# Revit family: 931-10-001 DN350-900
name_source: partatom
category: Pipe Accessories
units: mm (PartAtom-declared; Revit-internal decimal feet)

## family parameters
Always vertical = Yes
Cut with Voids When Loaded = No
Part Type = Valve - Breaks Into
Round Connector Dimension = Use Diameter
Shared = No
Work Plane-Based = No

## types (16) — shared parameters
1 = 1 mm  [stored 0.00328084 ft]
2 = 3 mm  [stored 0.00984252 ft]
Body_Thickness = 2 mm  [stored 0.00656168 ft]
DN350_PN10 = 931-350-10-010020200000
DN350_PN16 = 931-350-10-020020200000
DN400_PN10 = 931-400-10-010020200000
DN400_PN16 = 931-400-10-020020200000
DN500_PN10 = 931-500-10-010020200000
DN500_PN16 = 931-500-10-020020200000
DN600_PN10 = 931-600-10-010020200000
DN600_PN16 = 931-600-10-020020200000
DN700_PN10 = 931-700-10-010020200000
DN700_PN16 = 931-700-10-020020200000
DN750_PN10 = 931-750-10-010020200000
DN750_PN16 = 931-750-10-020020200000
DN800_PN10 = 931-800-10-010020200000
DN800_PN16 = 931-800-10-020020200000
DN900_PN10 = 931-900-10-010020200000
DN900_PN16 = 931-900-10-020020200000
Description_ = AVK BUTTERFLY VALVE, WAFER, PN10/16
Search_table = 931-10-001 DN350-900
URL_product_pages = https://www.avkvalves.com
zero-valued in all types: Default Elevation

## per-type parameters (varying)
- DN350_PN10: Actuator_FL_T=20 mm  [stored 0.0656168 ft]; Actuator_Flange_R=75 mm; B=174 mm; B1=175 mm; Body_dim=38 mm  [stored 0.124672 ft]; Body_dim1=55 mm  [stored 0.180446 ft]; Body_thickness=184 mm; Bore_R=175 mm; C=78 mm; D=213 mm; D1=426 mm; DN=350 mm; E=306 mm; F=32 mm  [stored 0.104987 ft]; Flange_R=200 mm; Flange_T=25 mm  [stored 0.082021 ft]; G=27 mm  [stored 0.0885827 ft]; H=88 mm; Hole=30 mm  [stored 0.0984252 ft]; Hole_dia=28 mm  [stored 0.0918635 ft]; PCD_R=235 mm; Rib_dim1=250 mm; base=27 mm  [stored 0.0885827 ft]; base1=16 mm; base_dis=247 mm; disk=14 mm  [stored 0.0459318 ft]; disk1=24 mm; disk2=348 mm; hole1=14 mm  [stored 0.0459318 ft]; hole_bottom=210 mm; rib2=235 mm; rubber=19 mm  [stored 0.062336 ft]; wafer=113 mm; wafer_F=40 mm  [stored 0.131234 ft]; wafer_dim1=25 mm  [stored 0.082021 ft]; wafer_dim2=113 mm; wafer_fillet=56 mm
- DN350_PN16: Actuator_FL_T=20 mm  [stored 0.0656168 ft]; Actuator_Flange_R=75 mm; B=174 mm; B1=175 mm; Body_dim=38 mm  [stored 0.124672 ft]; Body_dim1=55 mm  [stored 0.180446 ft]; Body_thickness=184 mm; Bore_R=175 mm; C=78 mm; D=213 mm; D1=426 mm; DN=350 mm; E=306 mm; F=32 mm  [stored 0.104987 ft]; Flange_R=200 mm; Flange_T=27 mm  [stored 0.0885827 ft]; G=27 mm  [stored 0.0885827 ft]; H=88 mm; Hole=30 mm  [stored 0.0984252 ft]; Hole_dia=28 mm  [stored 0.0918635 ft]; PCD_R=235 mm; Rib_dim1=250 mm; base=27 mm  [stored 0.0885827 ft]; base1=16 mm; base_dis=247 mm; disk=14 mm  [stored 0.0459318 ft]; disk1=24 mm; disk2=348 mm; hole1=14 mm  [stored 0.0459318 ft]; hole_bottom=210 mm; rib2=235 mm; rubber=19 mm  [stored 0.062336 ft]; wafer=113 mm; wafer_F=40 mm  [stored 0.131234 ft]; wafer_dim1=27 mm  [stored 0.0885827 ft]; wafer_dim2=113 mm; wafer_fillet=56 mm
- DN400_PN10: Actuator_FL_T=20 mm  [stored 0.0656168 ft]; Actuator_Flange_R=75 mm; B=195 mm; B1=196 mm; Body_dim=38 mm  [stored 0.124672 ft]; Body_dim1=71 mm; Body_thickness=206 mm; Bore_R=200 mm; C=102 mm; D=242 mm; D1=484 mm; DN=400 mm; E=328 mm; F=43 mm  [stored 0.141076 ft]; Flange_R=228 mm; Flange_T=25 mm  [stored 0.082021 ft]; G=27 mm  [stored 0.0885827 ft]; H=88 mm; Hole=30 mm  [stored 0.0984252 ft]; Hole_dia=28 mm  [stored 0.0918635 ft]; PCD_R=258 mm; Rib_dim1=295 mm; base=36 mm  [stored 0.11811 ft]; base1=20 mm  [stored 0.0656168 ft]; base_dis=279 mm; disk=14 mm  [stored 0.0459318 ft]; disk1=24 mm; disk2=390 mm; hole1=14 mm  [stored 0.0459318 ft]; hole_bottom=237 mm; rib2=265 mm; rubber=21 mm  [stored 0.0688976 ft]; wafer=113 mm; wafer_F=40 mm  [stored 0.131234 ft]; wafer_dim1=25 mm  [stored 0.082021 ft]; wafer_dim2=113 mm; wafer_fillet=56 mm
- DN400_PN16: Actuator_FL_T=20 mm  [stored 0.0656168 ft]; Actuator_Flange_R=75 mm; B=195 mm; B1=196 mm; Body_dim=38 mm  [stored 0.124672 ft]; Body_dim1=71 mm; Body_thickness=206 mm; Bore_R=200 mm; C=102 mm; D=242 mm; D1=484 mm; DN=400 mm; E=328 mm; F=43 mm  [stored 0.141076 ft]; Flange_R=230 mm; Flange_T=28 mm  [stored 0.0918635 ft]; G=27 mm  [stored 0.0885827 ft]; H=88 mm; Hole=30 mm  [stored 0.0984252 ft]; Hole_dia=28 mm  [stored 0.0918635 ft]; PCD_R=263 mm; Rib_dim1=295 mm; base=36 mm  [stored 0.11811 ft]; base1=20 mm  [stored 0.0656168 ft]; base_dis=279 mm; disk=14 mm  [stored 0.0459318 ft]; disk1=24 mm; disk2=390 mm; hole1=14 mm  [stored 0.0459318 ft]; hole_bottom=237 mm; rib2=265 mm; rubber=21 mm  [stored 0.0688976 ft]; wafer=113 mm; wafer_F=40 mm  [stored 0.131234 ft]; wafer_dim1=28 mm  [stored 0.0918635 ft]; wafer_dim2=113 mm; wafer_fillet=56 mm
- DN500_PN10: Actuator_FL_T=20 mm  [stored 0.0656168 ft]; Actuator_Flange_R=88 mm; B=246 mm; B1=247 mm; Body_dim=44 mm; Body_dim1=89 mm; Body_thickness=259 mm; Bore_R=250 mm; C=127 mm; D=299 mm; D1=597 mm; DN=500 mm; E=403 mm; F=39 mm  [stored 0.127953 ft]; Flange_R=285 mm; Flange_T=27 mm  [stored 0.0885827 ft]; G=36 mm  [stored 0.11811 ft]; H=105 mm; Hole=40 mm  [stored 0.131234 ft]; Hole_dia=31 mm  [stored 0.101706 ft]; PCD_R=310 mm; Rib_dim1=349 mm; base=44 mm; base1=25 mm  [stored 0.082021 ft]; base_dis=349 mm; disk=18 mm  [stored 0.0590551 ft]; disk1=32 mm  [stored 0.104987 ft]; disk2=492 mm; hole1=18 mm  [stored 0.0590551 ft]; hole_bottom=297 mm; rib2=332 mm; rubber=24 mm; wafer=131 mm; wafer_F=41 mm  [stored 0.134514 ft]; wafer_dim1=27 mm  [stored 0.0885827 ft]; wafer_dim2=131 mm; wafer_fillet=66 mm
- DN500_PN16: Actuator_FL_T=18 mm  [stored 0.0590551 ft]; Actuator_Flange_R=88 mm; B=246 mm; B1=247 mm; Body_dim=44 mm; Body_dim1=89 mm; Body_thickness=259 mm; Bore_R=250 mm; C=127 mm; D=299 mm; D1=597 mm; DN=500 mm; E=403 mm; F=39 mm  [stored 0.127953 ft]; Flange_R=300 mm; Flange_T=32 mm  [stored 0.104987 ft]; G=36 mm  [stored 0.11811 ft]; H=105 mm; Hole=40 mm  [stored 0.131234 ft]; Hole_dia=31 mm  [stored 0.101706 ft]; PCD_R=310 mm; Rib_dim1=349 mm; base=44 mm; base1=25 mm  [stored 0.082021 ft]; base_dis=349 mm; disk=18 mm  [stored 0.0590551 ft]; disk1=32 mm  [stored 0.104987 ft]; disk2=492 mm; hole1=18 mm  [stored 0.0590551 ft]; hole_bottom=297 mm; rib2=332 mm; rubber=24 mm; wafer=131 mm; wafer_F=41 mm  [stored 0.134514 ft]; wafer_dim1=32 mm  [stored 0.104987 ft]; wafer_dim2=131 mm; wafer_fillet=66 mm
- DN600_PN10: Actuator_FL_T=30 mm  [stored 0.0984252 ft]; Actuator_Flange_R=105 mm; B=289 mm; B1=290 mm; Body_dim=53 mm; Body_dim1=108 mm; Body_thickness=304 mm; Bore_R=300 mm; C=154 mm; D=359 mm; D1=717 mm; DN=600 mm; E=495 mm; F=68 mm; Flange_R=350 mm; Flange_T=30 mm  [stored 0.0984252 ft]; G=46 mm  [stored 0.150919 ft]; H=105 mm; Hole=51 mm; Hole_dia=31 mm  [stored 0.101706 ft]; PCD_R=363 mm; Rib_dim1=432 mm; base=54 mm; base1=31 mm  [stored 0.101706 ft]; base_dis=432 mm; disk=23 mm  [stored 0.0754593 ft]; disk1=41 mm  [stored 0.134514 ft]; disk2=577 mm; hole1=23 mm  [stored 0.0754593 ft]; hole_bottom=367 mm; rib2=410 mm; rubber=29 mm; wafer=158 mm; wafer_F=41 mm  [stored 0.134514 ft]; wafer_dim1=30 mm  [stored 0.0984252 ft]; wafer_dim2=158 mm; wafer_fillet=79 mm
- DN600_PN16: Actuator_FL_T=30 mm  [stored 0.0984252 ft]; Actuator_Flange_R=105 mm; B=289 mm; B1=290 mm; Body_dim=53 mm; Body_dim1=108 mm; Body_thickness=304 mm; Bore_R=300 mm; C=154 mm; D=359 mm; D1=717 mm; DN=600 mm; E=495 mm; F=68 mm; Flange_R=350 mm; Flange_T=36 mm  [stored 0.11811 ft]; G=46 mm  [stored 0.150919 ft]; H=105 mm; Hole=51 mm; Hole_dia=37 mm  [stored 0.121391 ft]; PCD_R=363 mm; Rib_dim1=432 mm; base=54 mm; base1=31 mm  [stored 0.101706 ft]; base_dis=432 mm; disk=23 mm  [stored 0.0754593 ft]; disk1=41 mm  [stored 0.134514 ft]; disk2=577 mm; hole1=23 mm  [stored 0.0754593 ft]; hole_bottom=367 mm; rib2=410 mm; rubber=29 mm; wafer=158 mm; wafer_F=41 mm  [stored 0.134514 ft]; wafer_dim1=36 mm  [stored 0.11811 ft]; wafer_dim2=158 mm; wafer_fillet=79 mm
- DN700_PN10: Actuator_FL_T=30 mm  [stored 0.0984252 ft]; Actuator_Flange_R=105 mm; B=341 mm; B1=342 mm; Body_dim=53 mm; Body_dim1=116 mm; Body_thickness=359 mm; Bore_R=350 mm; C=165 mm; D=397 mm; D1=793 mm; DN=700 mm; E=565 mm; F=68 mm; Flange_R=410 mm; Flange_T=33 mm  [stored 0.108268 ft]; G=46 mm  [stored 0.150919 ft]; H=105 mm; Hole=51 mm; Hole_dia=36 mm  [stored 0.11811 ft]; PCD_R=430 mm; Rib_dim1=500 mm; base=58 mm; base1=33 mm  [stored 0.108268 ft]; base_dis=500 mm; disk=23 mm  [stored 0.0754593 ft]; disk1=41 mm  [stored 0.134514 ft]; disk2=681 mm; hole1=23 mm  [stored 0.0754593 ft]; hole_bottom=425 mm; rib2=475 mm; rubber=23 mm  [stored 0.0754593 ft]; wafer=158 mm; wafer_F=45 mm  [stored 0.147638 ft]; wafer_dim1=33 mm  [stored 0.108268 ft]; wafer_dim2=158 mm; wafer_fillet=79 mm
- DN700_PN16: Actuator_FL_T=30 mm  [stored 0.0984252 ft]; Actuator_Flange_R=105 mm; B=341 mm; B1=342 mm; Body_dim=53 mm; Body_dim1=116 mm; Body_thickness=359 mm; Bore_R=350 mm; C=165 mm; D=397 mm; D1=793 mm; DN=700 mm; E=565 mm; F=68 mm; Flange_R=410 mm; Flange_T=40 mm  [stored 0.131234 ft]; G=46 mm  [stored 0.150919 ft]; H=105 mm; Hole=51 mm; Hole_dia=36 mm  [stored 0.11811 ft]; PCD_R=420 mm; Rib_dim1=500 mm; base=58 mm; base1=33 mm  [stored 0.108268 ft]; base_dis=500 mm; disk=23 mm  [stored 0.0754593 ft]; disk1=41 mm  [stored 0.134514 ft]; disk2=681 mm; hole1=23 mm  [stored 0.0754593 ft]; hole_bottom=425 mm; rib2=475 mm; rubber=23 mm  [stored 0.0754593 ft]; wafer=158 mm; wafer_F=45 mm  [stored 0.147638 ft]; wafer_dim1=40 mm  [stored 0.131234 ft]; wafer_dim2=158 mm; wafer_fillet=79 mm
- DN750_PN10: Actuator_FL_T=30 mm  [stored 0.0984252 ft]; Actuator_Flange_R=105 mm; B=372 mm; B1=373 mm; Body_dim=53 mm; Body_dim1=116 mm; Body_thickness=391 mm; Bore_R=375 mm; C=165 mm; D=438 mm; D1=875 mm; DN=750 mm; E=584 mm; F=68 mm; Flange_R=430 mm; Flange_T=40 mm  [stored 0.131234 ft]; G=46 mm  [stored 0.150919 ft]; H=105 mm; Hole=51 mm; Hole_dia=31 mm  [stored 0.101706 ft]; PCD_R=457 mm; Rib_dim1=500 mm; base=58 mm; base1=33 mm  [stored 0.108268 ft]; base_dis=530 mm; disk=23 mm  [stored 0.0754593 ft]; disk1=41 mm  [stored 0.134514 ft]; disk2=743 mm; hole1=23 mm  [stored 0.0754593 ft]; hole_bottom=451 mm; rib2=504 mm; rubber=31 mm  [stored 0.101706 ft]; wafer=158 mm; wafer_F=46 mm  [stored 0.150919 ft]; wafer_dim1=40 mm  [stored 0.131234 ft]; wafer_dim2=158 mm; wafer_fillet=79 mm
- DN750_PN16: Actuator_FL_T=30 mm  [stored 0.0984252 ft]; Actuator_Flange_R=105 mm; B=372 mm; B1=373 mm; Body_dim=53 mm; Body_dim1=116 mm; Body_thickness=391 mm; Bore_R=375 mm; C=165 mm; D=438 mm; D1=875 mm; DN=750 mm; E=584 mm; F=68 mm; Flange_R=425 mm; Flange_T=40 mm  [stored 0.131234 ft]; G=46 mm  [stored 0.150919 ft]; H=105 mm; Hole=51 mm; Hole_dia=31 mm  [stored 0.101706 ft]; PCD_R=457 mm; Rib_dim1=500 mm; base=58 mm; base1=33 mm  [stored 0.108268 ft]; base_dis=530 mm; disk=23 mm  [stored 0.0754593 ft]; disk1=41 mm  [stored 0.134514 ft]; disk2=743 mm; hole1=23 mm  [stored 0.0754593 ft]; hole_bottom=451 mm; rib2=504 mm; rubber=31 mm  [stored 0.101706 ft]; wafer=158 mm; wafer_F=46 mm  [stored 0.150919 ft]; wafer_dim1=40 mm  [stored 0.131234 ft]; wafer_dim2=158 mm; wafer_fillet=79 mm
- DN800_PN10: Actuator_FL_T=32 mm  [stored 0.104987 ft]; Actuator_Flange_R=150 mm; B=394 mm; B1=395 mm; Body_dim=75 mm; Body_dim1=133 mm; Body_thickness=414 mm; Bore_R=400 mm; C=190 mm; D=454 mm; D1=907 mm; DN=800 mm; E=645 mm; F=75 mm; Flange_R=460 mm; Flange_T=35 mm  [stored 0.114829 ft]; G=55 mm  [stored 0.180446 ft]; H=150 mm; Hole=61 mm; Hole_dia=34 mm  [stored 0.111549 ft]; PCD_R=475 mm; Rib_dim1=540 mm; base=67 mm; base1=38 mm  [stored 0.124672 ft]; base_dis=551 mm; disk=28 mm  [stored 0.0918635 ft]; disk1=50 mm; disk2=787 mm; hole1=28 mm  [stored 0.0918635 ft]; hole_bottom=468 mm; rib2=523 mm; rubber=27 mm  [stored 0.0885827 ft]; wafer=225 mm; wafer_F=72 mm; wafer_dim1=35 mm  [stored 0.114829 ft]; wafer_dim2=225 mm; wafer_fillet=113 mm
- DN800_PN16: Actuator_FL_T=32 mm  [stored 0.104987 ft]; Actuator_Flange_R=150 mm; B=394 mm; B1=395 mm; Body_dim=75 mm; Body_dim1=133 mm; Body_thickness=414 mm; Bore_R=400 mm; C=190 mm; D=454 mm; D1=907 mm; DN=800 mm; E=645 mm; F=75 mm; Flange_R=465 mm; Flange_T=43 mm  [stored 0.141076 ft]; G=55 mm  [stored 0.180446 ft]; H=150 mm; Hole=61 mm; Hole_dia=34 mm  [stored 0.111549 ft]; PCD_R=475 mm; Rib_dim1=540 mm; base=67 mm; base1=38 mm  [stored 0.124672 ft]; base_dis=551 mm; disk=28 mm  [stored 0.0918635 ft]; disk1=50 mm; disk2=787 mm; hole1=28 mm  [stored 0.0918635 ft]; hole_bottom=468 mm; rib2=523 mm; rubber=27 mm  [stored 0.0885827 ft]; wafer=225 mm; wafer_F=72 mm; wafer_dim1=43 mm  [stored 0.141076 ft]; wafer_dim2=225 mm; wafer_fillet=113 mm
- DN900_PN10: Actuator_FL_T=35 mm  [stored 0.114829 ft]; Actuator_Flange_R=150 mm; B=450 mm; B1=451 mm; Body_dim=75 mm; Body_dim1=140 mm; Body_thickness=473 mm; Bore_R=450 mm; C=200 mm; D=524 mm; D1=1048 mm; DN=900 mm; E=705 mm; F=75 mm; Flange_R=520 mm; Flange_T=38 mm  [stored 0.124672 ft]; G=55 mm  [stored 0.180446 ft]; H=150 mm; Hole=61 mm; Hole_dia=36 mm  [stored 0.11811 ft]; PCD_R=543 mm; Rib_dim1=580 mm; base=70 mm; base1=40 mm  [stored 0.131234 ft]; base_dis=636 mm; disk=28 mm  [stored 0.0918635 ft]; disk1=50 mm; disk2=899 mm; hole1=28 mm  [stored 0.0918635 ft]; hole_bottom=541 mm; rib2=604 mm; rubber=37 mm  [stored 0.121391 ft]; wafer=225 mm; wafer_F=67 mm; wafer_dim1=38 mm  [stored 0.124672 ft]; wafer_dim2=225 mm; wafer_fillet=113 mm
- DN900_PN16: Actuator_FL_T=35 mm  [stored 0.114829 ft]; Actuator_Flange_R=150 mm; B=450 mm; B1=451 mm; Body_dim=75 mm; Body_dim1=140 mm; Body_thickness=473 mm; Bore_R=450 mm; C=200 mm; D=524 mm; D1=1048 mm; DN=900 mm; E=705 mm; F=75 mm; Flange_R=525 mm; Flange_T=47 mm; G=55 mm  [stored 0.180446 ft]; H=150 mm; Hole=61 mm; Hole_dia=36 mm  [stored 0.11811 ft]; PCD_R=543 mm; Rib_dim1=580 mm; base=70 mm; base1=40 mm  [stored 0.131234 ft]; base_dis=636 mm; disk=28 mm  [stored 0.0918635 ft]; disk1=50 mm; disk2=899 mm; hole1=28 mm  [stored 0.0918635 ft]; hole_bottom=541 mm; rib2=604 mm; rubber=37 mm  [stored 0.121391 ft]; wafer=225 mm; wafer_F=67 mm; wafer_dim1=47 mm; wafer_dim2=225 mm; wafer_fillet=113 mm

note: [stored X ft] marks values corroborated as IEEE doubles in the binary element streams (Revit-internal decimal feet)

## geometry (parser evidence)
native form markers: Sweep x5
no freeform markers — native parametric forms only
